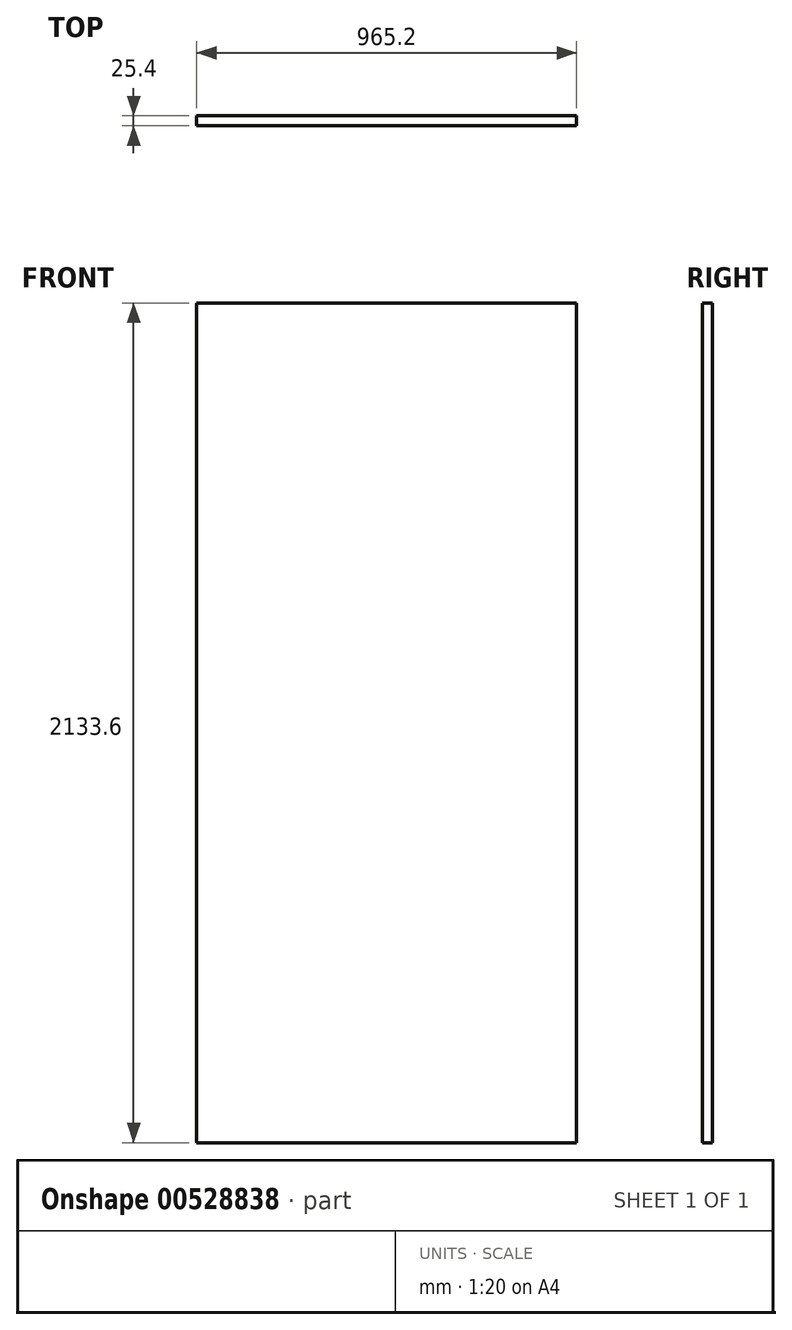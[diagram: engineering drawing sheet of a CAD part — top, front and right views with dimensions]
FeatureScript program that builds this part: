
annotation { "Feature Type Name" : "Feature", "Feature Type Description" : "" }
export const myFeature = defineFeature(function(context is Context, id is Id, definition is map)
    precondition{}
    {
        {
            var Q0;
            Q0=qCreatedBy(makeId("Front.planeOp"),FACE);
            var sketch = newSketch(context, id + "F0", { "sketchPlane" : qUnion([Q0])});
            skLineSegment(sketch, "E0.bottom", {"start": v(482.6, -1066.8) * mm, "end": v(0, -1066.8) * mm});
            skLineSegment(sketch, "E0.top", {"start": v(482.6, 1066.8) * mm, "end": v(0, 1066.8) * mm});
            skLineSegment(sketch, "E0.left", {"start": v(482.6, -1066.8) * mm, "end": v(482.6, 1066.8) * mm});
            skLineSegment(sketch, "E0.right", {"start": v(-482.6, -1066.8) * mm, "end": v(-482.6, 1066.8) * mm});
            skPoint(sketch, "E0.middle", {"position": v(0, 0) * mm});
            skLineSegment(sketch, "E1", {"start": v(0, 1066.8) * mm, "end": v(-482.6, 1066.8) * mm});
            skLineSegment(sketch, "E2", {"start": v(0, -1066.8) * mm, "end": v(-482.6, -1066.8) * mm});
            skLineSegment(sketch, "E3", {"start": v(0, 1066.8) * mm, "end": v(0, -1066.8) * mm});
            skLineSegment(sketch, "E4", {"start": v(0, 1066.8) * mm, "end": v(-482.6, 584.2) * mm});
            skLineSegment(sketch, "E5.1.0.0", {"start": v(0, 923.04) * mm, "end": v(-482.6, 440.44) * mm});
            skLineSegment(sketch, "E5.2.0.0", {"start": v(0, 779.27) * mm, "end": v(-482.6, 296.67) * mm});
            skLineSegment(sketch, "E5.3.0.0", {"start": v(0, 635.5) * mm, "end": v(-482.6, 152.9) * mm});
            skLineSegment(sketch, "E5.4.0.0", {"start": v(0, 491.74) * mm, "end": v(-482.6, 9.14) * mm});
            skLineSegment(sketch, "E5.5.0.0", {"start": v(0, 347.98) * mm, "end": v(-482.6, -134.62) * mm});
            skLineSegment(sketch, "E5.6.0.0", {"start": v(0, 204.22) * mm, "end": v(-482.6, -278.38) * mm});
            skLineSegment(sketch, "E5.7.0.0", {"start": v(0, 60.45) * mm, "end": v(-482.6, -422.15) * mm});
            skLineSegment(sketch, "E5.8.0.0", {"start": v(0, -83.31) * mm, "end": v(-482.6, -565.91) * mm});
            skLineSegment(sketch, "E5.9.0.0", {"start": v(0, -227.08) * mm, "end": v(-482.6, -709.68) * mm});
            skLineSegment(sketch, "E5.10.0.0", {"start": v(0, -370.84) * mm, "end": v(-482.6, -853.44) * mm});
            skLineSegment(sketch, "E5.11.0.0", {"start": v(0, -514.6) * mm, "end": v(-482.6, -997.2) * mm});
            skLineSegment(sketch, "E5.12.0.0", {"start": v(0, -658.37) * mm, "end": v(-408.43, -1066.8) * mm});
            skLineSegment(sketch, "E5.13.0.0", {"start": v(0, -802.13) * mm, "end": v(-264.67, -1066.8) * mm});
            skLineSegment(sketch, "E5.14.0.0", {"start": v(0, -945.9) * mm, "end": v(-120.9, -1066.8) * mm});
            skLineSegment(sketch, "E5.direction1", {"start": v(-482.6, 584.2) * mm, "end": v(-482.6, 440.44) * mm, "construction": true});
            skPoint(sketch, "E6.orphan", {"position": v(-482.6, -1428.5) * mm});
            skPoint(sketch, "E7.orphan", {"position": v(-482.6, -1284.73) * mm});
            skPoint(sketch, "E8.orphan", {"position": v(-482.6, -1140.97) * mm});
            skLineSegment(sketch, "E9.1.0.0", {"start": v(-143.76, 1066.8) * mm, "end": v(-482.6, 727.96) * mm});
            skLineSegment(sketch, "E9.2.0.0", {"start": v(-287.53, 1066.8) * mm, "end": v(-482.6, 871.73) * mm});
            skLineSegment(sketch, "E9.3.0.0", {"start": v(-431.3, 1066.8) * mm, "end": v(-482.6, 1015.5) * mm});
            skLineSegment(sketch, "E9.direction1", {"start": v(-482.6, 584.2) * mm, "end": v(-626.36, 584.2) * mm, "construction": true});
            skPoint(sketch, "E10.orphan", {"position": v(-913.9, 584.2) * mm});
            skPoint(sketch, "E11.orphan", {"position": v(-770.13, 584.2) * mm});
            skLineSegment(sketch, "E12", {"start": v(0, 1066.8) * mm, "end": v(482.6, 584.2) * mm});
            skLineSegment(sketch, "E13.1.0.0", {"start": v(143.76, 1066.8) * mm, "end": v(482.6, 727.96) * mm});
            skLineSegment(sketch, "E13.2.0.0", {"start": v(287.53, 1066.8) * mm, "end": v(482.6, 871.73) * mm});
            skLineSegment(sketch, "E13.3.0.0", {"start": v(431.3, 1066.8) * mm, "end": v(482.6, 1015.5) * mm});
            skLineSegment(sketch, "E13.direction1", {"start": v(0, 1066.8) * mm, "end": v(143.76, 1066.8) * mm, "construction": true});
            skPoint(sketch, "E14.orphan", {"position": v(913.9, 584.2) * mm});
            skPoint(sketch, "E15.orphan", {"position": v(770.13, 584.2) * mm});
            skPoint(sketch, "E16.orphan", {"position": v(626.36, 584.2) * mm});
            skLineSegment(sketch, "E17.1.0.0", {"start": v(0, 923.04) * mm, "end": v(482.6, 440.44) * mm});
            skLineSegment(sketch, "E17.2.0.0", {"start": v(0, 779.27) * mm, "end": v(482.6, 296.67) * mm});
            skLineSegment(sketch, "E17.3.0.0", {"start": v(0, 635.5) * mm, "end": v(482.6, 152.9) * mm});
            skLineSegment(sketch, "E17.4.0.0", {"start": v(0, 491.74) * mm, "end": v(482.6, 9.14) * mm});
            skLineSegment(sketch, "E17.5.0.0", {"start": v(0, 347.98) * mm, "end": v(482.6, -134.62) * mm});
            skLineSegment(sketch, "E17.6.0.0", {"start": v(0, 204.22) * mm, "end": v(482.6, -278.38) * mm});
            skLineSegment(sketch, "E17.7.0.0", {"start": v(0, 60.45) * mm, "end": v(482.6, -422.15) * mm});
            skLineSegment(sketch, "E17.8.0.0", {"start": v(0, -83.31) * mm, "end": v(482.6, -565.91) * mm});
            skLineSegment(sketch, "E17.9.0.0", {"start": v(0, -227.08) * mm, "end": v(482.6, -709.68) * mm});
            skLineSegment(sketch, "E17.10.0.0", {"start": v(0, -370.84) * mm, "end": v(482.6, -853.44) * mm});
            skLineSegment(sketch, "E17.11.0.0", {"start": v(0, -514.6) * mm, "end": v(482.6, -997.2) * mm});
            skLineSegment(sketch, "E17.12.0.0", {"start": v(0, -658.37) * mm, "end": v(408.43, -1066.8) * mm});
            skLineSegment(sketch, "E17.13.0.0", {"start": v(0, -802.13) * mm, "end": v(264.67, -1066.8) * mm});
            skLineSegment(sketch, "E17.14.0.0", {"start": v(0, -945.9) * mm, "end": v(120.9, -1066.8) * mm});
            skLineSegment(sketch, "E17.direction1", {"start": v(0, 1066.8) * mm, "end": v(0, 923.04) * mm, "construction": true});
            skPoint(sketch, "E18.orphan", {"position": v(482.6, -1428.5) * mm});
            skPoint(sketch, "E19.orphan", {"position": v(482.6, -1284.73) * mm});
            skPoint(sketch, "E20.orphan", {"position": v(482.6, -1140.97) * mm});
            skSolve(sketch);
        }
        {
            var Q0;
            {var subQ0=sQuery(id+"F0.wireOp",EDGE,"E17.2.0.0");Q0=makeQuery(id+"F0.imprint","IMPRINT",FACE,{"disambiguationData":[TD([[makeQuery(id+"F0.imprint","IMPRINT",EDGE,{"derivedFrom":subQ0}),-1.0]])]});}
            var Q1;
            {var subQ0=sQuery(id+"F0.wireOp",EDGE,"E5.1.0.0");Q1=makeQuery(id+"F0.imprint","IMPRINT",FACE,{"disambiguationData":[TD([[makeQuery(id+"F0.imprint","IMPRINT",EDGE,{"derivedFrom":subQ0}),1.0]])]});}
            var Q2;
            {var subQ0=sQuery(id+"F0.wireOp",EDGE,"E12");Q2=makeQuery(id+"F0.imprint","IMPRINT",FACE,{"disambiguationData":[TD([[makeQuery(id+"F0.imprint","IMPRINT",EDGE,{"derivedFrom":subQ0}),1.0]])]});}
            var Q3;
            {var subQ0=sQuery(id+"F0.wireOp",EDGE,"E4");Q3=makeQuery(id+"F0.imprint","IMPRINT",FACE,{"disambiguationData":[TD([[makeQuery(id+"F0.imprint","IMPRINT",EDGE,{"derivedFrom":subQ0}),-1.0]])]});}
            var Q4;
            {var subQ0=sQuery(id+"F0.wireOp",EDGE,"E4");Q4=makeQuery(id+"F0.imprint","IMPRINT",FACE,{"disambiguationData":[TD([[makeQuery(id+"F0.imprint","IMPRINT",EDGE,{"derivedFrom":subQ0}),1.0]])]});}
            var Q5;
            {var subQ0=sQuery(id+"F0.wireOp",EDGE,"E9.1.0.0");Q5=makeQuery(id+"F0.imprint","IMPRINT",FACE,{"disambiguationData":[TD([[makeQuery(id+"F0.imprint","IMPRINT",EDGE,{"derivedFrom":subQ0}),-1.0]])]});}
            var Q6;
            {var subQ0=sQuery(id+"F0.wireOp",EDGE,"E5.2.0.0");Q6=makeQuery(id+"F0.imprint","IMPRINT",FACE,{"disambiguationData":[TD([[makeQuery(id+"F0.imprint","IMPRINT",EDGE,{"derivedFrom":subQ0}),1.0]])]});}
            var Q7;
            {var subQ0=sQuery(id+"F0.wireOp",EDGE,"E17.1.0.0");Q7=makeQuery(id+"F0.imprint","IMPRINT",FACE,{"disambiguationData":[TD([[makeQuery(id+"F0.imprint","IMPRINT",EDGE,{"derivedFrom":subQ0}),-1.0]])]});}
            var Q8;
            {var subQ0=sQuery(id+"F0.wireOp",EDGE,"E13.1.0.0");Q8=makeQuery(id+"F0.imprint","IMPRINT",FACE,{"disambiguationData":[TD([[makeQuery(id+"F0.imprint","IMPRINT",EDGE,{"derivedFrom":subQ0}),1.0]])]});}
            var Q9;
            {var subQ3=sQuery(id+"F0.wireOp",EDGE,"E13.3.0.0");Q9=makeQuery(id+"F0.imprint","IMPRINT",FACE,{"disambiguationData":[TD([[makeQuery(id+"F0.imprint","IMPRINT",EDGE,{"derivedFrom":subQ3}),1.0]])]});}
            var Q10;
            {var subQ3=sQuery(id+"F0.wireOp",EDGE,"E9.3.0.0");Q10=makeQuery(id+"F0.imprint","IMPRINT",FACE,{"disambiguationData":[TD([[makeQuery(id+"F0.imprint","IMPRINT",EDGE,{"derivedFrom":subQ3}),-1.0]])]});}
            var Q11;
            {var subQ0=sQuery(id+"F0.wireOp",EDGE,"E9.2.0.0");Q11=makeQuery(id+"F0.imprint","IMPRINT",FACE,{"disambiguationData":[TD([[makeQuery(id+"F0.imprint","IMPRINT",EDGE,{"derivedFrom":subQ0}),-1.0]])]});}
            var Q12;
            {var subQ0=sQuery(id+"F0.wireOp",EDGE,"E13.2.0.0");Q12=makeQuery(id+"F0.imprint","IMPRINT",FACE,{"disambiguationData":[TD([[makeQuery(id+"F0.imprint","IMPRINT",EDGE,{"derivedFrom":subQ0}),1.0]])]});}
            var Q13;
            {var subQ0=sQuery(id+"F0.wireOp",EDGE,"E12");Q13=makeQuery(id+"F0.imprint","IMPRINT",FACE,{"disambiguationData":[TD([[makeQuery(id+"F0.imprint","IMPRINT",EDGE,{"derivedFrom":subQ0}),-1.0]])]});}
            var Q14;
            {var subQ0=sQuery(id+"F0.wireOp",EDGE,"E17.3.0.0");Q14=makeQuery(id+"F0.imprint","IMPRINT",FACE,{"disambiguationData":[TD([[makeQuery(id+"F0.imprint","IMPRINT",EDGE,{"derivedFrom":subQ0}),-1.0]])]});}
            var Q15;
            {var subQ0=sQuery(id+"F0.wireOp",EDGE,"E5.3.0.0");Q15=makeQuery(id+"F0.imprint","IMPRINT",FACE,{"disambiguationData":[TD([[makeQuery(id+"F0.imprint","IMPRINT",EDGE,{"derivedFrom":subQ0}),1.0]])]});}
            var Q16;
            {var subQ0=sQuery(id+"F0.wireOp",EDGE,"E5.4.0.0");Q16=makeQuery(id+"F0.imprint","IMPRINT",FACE,{"disambiguationData":[TD([[makeQuery(id+"F0.imprint","IMPRINT",EDGE,{"derivedFrom":subQ0}),1.0]])]});}
            var Q17;
            {var subQ0=sQuery(id+"F0.wireOp",EDGE,"E5.5.0.0");Q17=makeQuery(id+"F0.imprint","IMPRINT",FACE,{"disambiguationData":[TD([[makeQuery(id+"F0.imprint","IMPRINT",EDGE,{"derivedFrom":subQ0}),1.0]])]});}
            var Q18;
            {var subQ0=sQuery(id+"F0.wireOp",EDGE,"E5.6.0.0");Q18=makeQuery(id+"F0.imprint","IMPRINT",FACE,{"disambiguationData":[TD([[makeQuery(id+"F0.imprint","IMPRINT",EDGE,{"derivedFrom":subQ0}),1.0]])]});}
            var Q19;
            {var subQ0=sQuery(id+"F0.wireOp",EDGE,"E5.7.0.0");Q19=makeQuery(id+"F0.imprint","IMPRINT",FACE,{"disambiguationData":[TD([[makeQuery(id+"F0.imprint","IMPRINT",EDGE,{"derivedFrom":subQ0}),1.0]])]});}
            var Q20;
            {var subQ0=sQuery(id+"F0.wireOp",EDGE,"E5.8.0.0");Q20=makeQuery(id+"F0.imprint","IMPRINT",FACE,{"disambiguationData":[TD([[makeQuery(id+"F0.imprint","IMPRINT",EDGE,{"derivedFrom":subQ0}),1.0]])]});}
            var Q21;
            {var subQ0=sQuery(id+"F0.wireOp",EDGE,"E5.9.0.0");Q21=makeQuery(id+"F0.imprint","IMPRINT",FACE,{"disambiguationData":[TD([[makeQuery(id+"F0.imprint","IMPRINT",EDGE,{"derivedFrom":subQ0}),1.0]])]});}
            var Q22;
            {var subQ0=sQuery(id+"F0.wireOp",EDGE,"E5.10.0.0");Q22=makeQuery(id+"F0.imprint","IMPRINT",FACE,{"disambiguationData":[TD([[makeQuery(id+"F0.imprint","IMPRINT",EDGE,{"derivedFrom":subQ0}),1.0]])]});}
            var Q23;
            {var subQ4=sQuery(id+"F0.wireOp",EDGE,"E5.11.0.0");Q23=makeQuery(id+"F0.imprint","IMPRINT",FACE,{"disambiguationData":[TD([[makeQuery(id+"F0.imprint","IMPRINT",EDGE,{"derivedFrom":subQ4}),1.0]])]});}
            var Q24;
            {var subQ0=sQuery(id+"F0.wireOp",EDGE,"E5.13.0.0");Q24=makeQuery(id+"F0.imprint","IMPRINT",FACE,{"disambiguationData":[TD([[makeQuery(id+"F0.imprint","IMPRINT",EDGE,{"derivedFrom":subQ0}),1.0]])]});}
            var Q25;
            {var subQ3=sQuery(id+"F0.wireOp",EDGE,"E5.14.0.0");Q25=makeQuery(id+"F0.imprint","IMPRINT",FACE,{"disambiguationData":[TD([[makeQuery(id+"F0.imprint","IMPRINT",EDGE,{"derivedFrom":subQ3}),1.0]])]});}
            var Q26;
            {var subQ0=sQuery(id+"F0.wireOp",EDGE,"E17.4.0.0");Q26=makeQuery(id+"F0.imprint","IMPRINT",FACE,{"disambiguationData":[TD([[makeQuery(id+"F0.imprint","IMPRINT",EDGE,{"derivedFrom":subQ0}),-1.0]])]});}
            var Q27;
            {var subQ0=sQuery(id+"F0.wireOp",EDGE,"E17.5.0.0");Q27=makeQuery(id+"F0.imprint","IMPRINT",FACE,{"disambiguationData":[TD([[makeQuery(id+"F0.imprint","IMPRINT",EDGE,{"derivedFrom":subQ0}),-1.0]])]});}
            var Q28;
            {var subQ0=sQuery(id+"F0.wireOp",EDGE,"E17.6.0.0");Q28=makeQuery(id+"F0.imprint","IMPRINT",FACE,{"disambiguationData":[TD([[makeQuery(id+"F0.imprint","IMPRINT",EDGE,{"derivedFrom":subQ0}),-1.0]])]});}
            var Q29;
            {var subQ0=sQuery(id+"F0.wireOp",EDGE,"E17.7.0.0");Q29=makeQuery(id+"F0.imprint","IMPRINT",FACE,{"disambiguationData":[TD([[makeQuery(id+"F0.imprint","IMPRINT",EDGE,{"derivedFrom":subQ0}),-1.0]])]});}
            var Q30;
            {var subQ0=sQuery(id+"F0.wireOp",EDGE,"E17.8.0.0");Q30=makeQuery(id+"F0.imprint","IMPRINT",FACE,{"disambiguationData":[TD([[makeQuery(id+"F0.imprint","IMPRINT",EDGE,{"derivedFrom":subQ0}),-1.0]])]});}
            var Q31;
            {var subQ0=sQuery(id+"F0.wireOp",EDGE,"E17.9.0.0");Q31=makeQuery(id+"F0.imprint","IMPRINT",FACE,{"disambiguationData":[TD([[makeQuery(id+"F0.imprint","IMPRINT",EDGE,{"derivedFrom":subQ0}),-1.0]])]});}
            var Q32;
            {var subQ0=sQuery(id+"F0.wireOp",EDGE,"E17.10.0.0");Q32=makeQuery(id+"F0.imprint","IMPRINT",FACE,{"disambiguationData":[TD([[makeQuery(id+"F0.imprint","IMPRINT",EDGE,{"derivedFrom":subQ0}),-1.0]])]});}
            var Q33;
            {var subQ0=sQuery(id+"F0.wireOp",EDGE,"E17.11.0.0");Q33=makeQuery(id+"F0.imprint","IMPRINT",FACE,{"disambiguationData":[TD([[makeQuery(id+"F0.imprint","IMPRINT",EDGE,{"derivedFrom":subQ0}),-1.0]])]});}
            var Q34;
            {var subQ0=sQuery(id+"F0.wireOp",EDGE,"E17.12.0.0");Q34=makeQuery(id+"F0.imprint","IMPRINT",FACE,{"disambiguationData":[TD([[makeQuery(id+"F0.imprint","IMPRINT",EDGE,{"derivedFrom":subQ0}),-1.0]])]});}
            var Q35;
            {var subQ0=sQuery(id+"F0.wireOp",EDGE,"E17.13.0.0");Q35=makeQuery(id+"F0.imprint","IMPRINT",FACE,{"disambiguationData":[TD([[makeQuery(id+"F0.imprint","IMPRINT",EDGE,{"derivedFrom":subQ0}),-1.0]])]});}
            var Q36;
            {var subQ3=sQuery(id+"F0.wireOp",EDGE,"E17.14.0.0");Q36=makeQuery(id+"F0.imprint","IMPRINT",FACE,{"disambiguationData":[TD([[makeQuery(id+"F0.imprint","IMPRINT",EDGE,{"derivedFrom":subQ3}),-1.0]])]});}
            var Q37;
            {var subQ0=sQuery(id+"F0.wireOp",EDGE,"E5.12.0.0");Q37=makeQuery(id+"F0.imprint","IMPRINT",FACE,{"disambiguationData":[TD([[makeQuery(id+"F0.imprint","IMPRINT",EDGE,{"derivedFrom":subQ0}),1.0]])]});}
            var Q38;
            Q38=sQuery(id+"F0.wireOp",EDGE,"E0.left");
            var Q39;
            Q39=sQuery(id+"F0.wireOp",EDGE,"E13.2.0.0");
            var Q40;
            Q40=sQuery(id+"F0.wireOp",EDGE,"E13.1.0.0");
            var Q41;
            Q41=sQuery(id+"F0.wireOp",EDGE,"E1");
            var Q42;
            Q42=sQuery(id+"F0.wireOp",EDGE,"E0.top");
            var Q43;
            Q43=sQuery(id+"F0.wireOp",EDGE,"E0.right");
            var Q44;
            Q44=sQuery(id+"F0.wireOp",EDGE,"E3");
            var Q45;
            Q45=sQuery(id+"F0.wireOp",EDGE,"E9.2.0.0");
            var Q46;
            Q46=sQuery(id+"F0.wireOp",EDGE,"E9.1.0.0");
            var Q47;
            Q47=sQuery(id+"F0.wireOp",EDGE,"E4");
            var Q48;
            Q48=sQuery(id+"F0.wireOp",EDGE,"E5.1.0.0");
            var Q49;
            Q49=sQuery(id+"F0.wireOp",EDGE,"E12");
            var Q50;
            Q50=sQuery(id+"F0.wireOp",EDGE,"E17.1.0.0");
            var Q51;
            Q51=sQuery(id+"F0.wireOp",EDGE,"E17.2.0.0");
            var Q52;
            Q52=sQuery(id+"F0.wireOp",EDGE,"E5.2.0.0");
            var Q53;
            Q53=sQuery(id+"F0.wireOp",EDGE,"E5.3.0.0");
            var Q54;
            Q54=sQuery(id+"F0.wireOp",EDGE,"E17.3.0.0");
            var Q55;
            Q55=sQuery(id+"F0.wireOp",EDGE,"E17.4.0.0");
            var Q56;
            Q56=sQuery(id+"F0.wireOp",EDGE,"E17.5.0.0");
            var Q57;
            Q57=sQuery(id+"F0.wireOp",EDGE,"E17.6.0.0");
            var Q58;
            Q58=sQuery(id+"F0.wireOp",EDGE,"E5.4.0.0");
            var Q59;
            Q59=sQuery(id+"F0.wireOp",EDGE,"E5.5.0.0");
            var Q60;
            Q60=sQuery(id+"F0.wireOp",EDGE,"E5.7.0.0");
            var Q61;
            Q61=sQuery(id+"F0.wireOp",EDGE,"E17.7.0.0");
            var Q62;
            Q62=sQuery(id+"F0.wireOp",EDGE,"E17.8.0.0");
            var Q63;
            Q63=sQuery(id+"F0.wireOp",EDGE,"E17.9.0.0");
            var Q64;
            Q64=sQuery(id+"F0.wireOp",EDGE,"E5.6.0.0");
            var Q65;
            Q65=sQuery(id+"F0.wireOp",EDGE,"E5.8.0.0");
            var Q66;
            Q66=sQuery(id+"F0.wireOp",EDGE,"E5.9.0.0");
            var Q67;
            Q67=sQuery(id+"F0.wireOp",EDGE,"E17.10.0.0");
            var Q68;
            Q68=sQuery(id+"F0.wireOp",EDGE,"E17.11.0.0");
            var Q69;
            Q69=sQuery(id+"F0.wireOp",EDGE,"E5.10.0.0");
            var Q70;
            Q70=sQuery(id+"F0.wireOp",EDGE,"E5.11.0.0");
            var Q71;
            Q71=sQuery(id+"F0.wireOp",EDGE,"E5.12.0.0");
            var Q72;
            Q72=sQuery(id+"F0.wireOp",EDGE,"E17.12.0.0");
            var Q73;
            Q73=sQuery(id+"F0.wireOp",EDGE,"E17.13.0.0");
            var Q74;
            Q74=sQuery(id+"F0.wireOp",EDGE,"E17.14.0.0");
            var Q75;
            Q75=sQuery(id+"F0.wireOp",EDGE,"E5.13.0.0");
            var Q76;
            Q76=sQuery(id+"F0.wireOp",EDGE,"E5.14.0.0");
            var Q77;
            Q77=sQuery(id+"F0.wireOp",EDGE,"E2");
            var Q78;
            Q78=sQuery(id+"F0.wireOp",EDGE,"E0.bottom");
            extrude(context, id + "F1", {"entities" : qUnion([Q0, Q1, Q2, Q3, Q4, Q5, Q6, Q7, Q8, Q9, Q10, Q11, Q12, Q13, Q14, Q15, Q16, Q17, Q18, Q19, Q20, Q21, Q22, Q23, Q24, Q25, Q26, Q27, Q28, Q29, Q30, Q31, Q32, Q33, Q34, Q35, Q36, Q37]), "surfaceEntities" : qUnion([Q38, Q39, Q40, Q41, Q42, Q43, Q44, Q45, Q46, Q47, Q48, Q49, Q50, Q51, Q52, Q53, Q54, Q55, Q56, Q57, Q58, Q59, Q60, Q61, Q62, Q63, Q64, Q65, Q66, Q67, Q68, Q69, Q70, Q71, Q72, Q73, Q74, Q75, Q76, Q77, Q78]), "depth" : 25.4 * mm, "offsetDistance" : 25.4 * mm});
        }
    });
